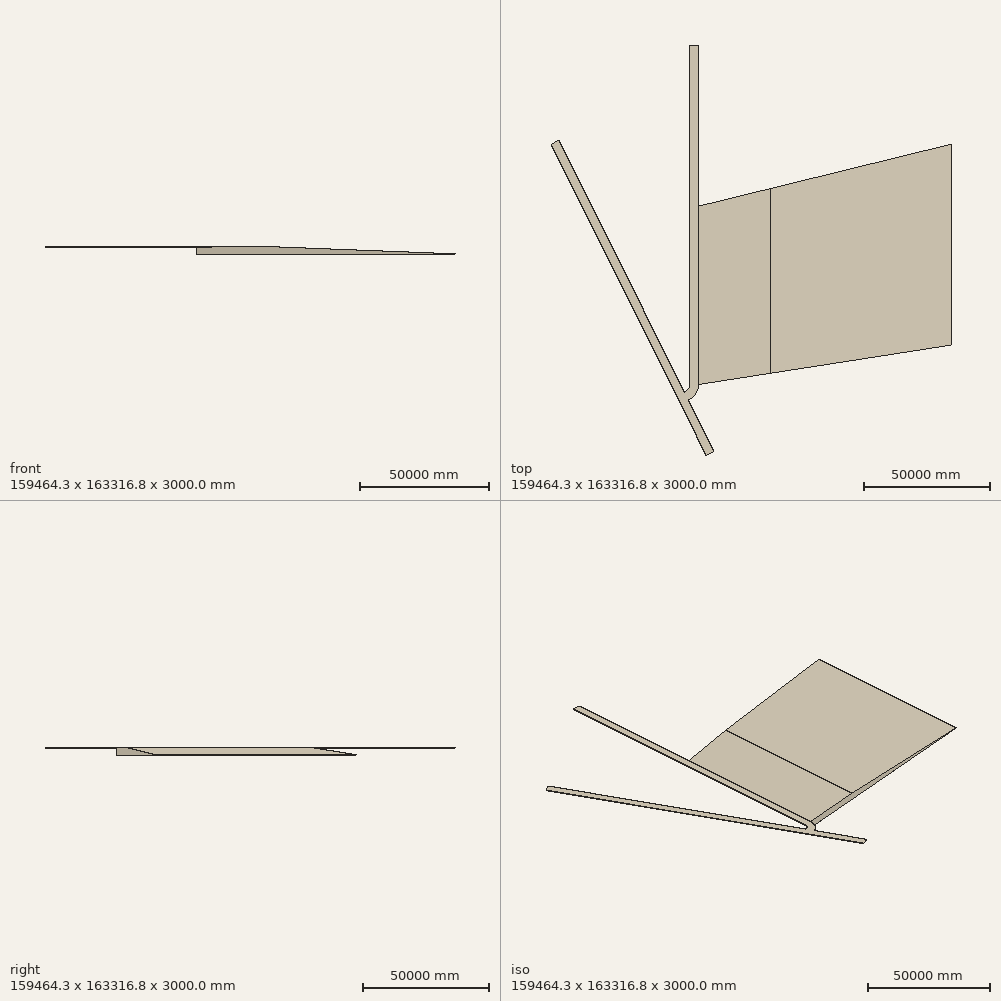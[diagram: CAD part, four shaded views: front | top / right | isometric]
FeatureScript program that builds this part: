
annotation { "Feature Type Name" : "Feature", "Feature Type Description" : "" }
export const myFeature = defineFeature(function(context is Context, id is Id, definition is map)
    precondition{}
    {
        {
            var Q0;
            Q0=qCreatedBy(makeId("Top.planeOp"),FACE);
            var sketch = newSketch(context, id + "F0", { "sketchPlane" : qUnion([Q0])});
            skLineSegment(sketch, "E0", {"start": v(0, 0) * mm, "end": v(0, 71000) * mm});
            skLineSegment(sketch, "E1", {"start": v(0, 0) * mm, "end": v(100779.6, 15731.25) * mm});
            skLineSegment(sketch, "E2", {"start": v(100779.6, 15731.25) * mm, "end": v(100779.6, 95731.25) * mm});
            skLineSegment(sketch, "E3", {"start": v(0, 71000) * mm, "end": v(100779.6, 95731.25) * mm});
            skLineSegment(sketch, "E4", {"start": v(0, 135054.72) * mm, "end": v(0, 71000) * mm});
            skArc(sketch, "E5", {"start": v(-4052.26, -6248.58) * mm, "mid": v(-1101.75, -3723.76) * mm, "end": v(0, 0) * mm});
            skLineSegment(sketch, "E6", {"start": v(-4052.26, -6248.58) * mm, "end": v(6144.3, -26700.48) * mm});
            skLineSegment(sketch, "E7", {"start": v(-3500, 18720.75) * mm, "end": v(-3500, 5971.3) * mm});
            skArc(sketch, "E8", {"start": v(-5616.78, -3110.52) * mm, "mid": v(-4079.4, -1881.23) * mm, "end": v(-3500, 0) * mm});
            skLineSegment(sketch, "E9", {"start": v(-3500, 5971.3) * mm, "end": v(-3500, 0) * mm});
            skLineSegment(sketch, "E10", {"start": v(-3500, 18720.75) * mm, "end": v(-3500, 135054.72) * mm});
            skLineSegment(sketch, "E11", {"start": v(6144.3, -26700.48) * mm, "end": v(3012.01, -28262.12) * mm});
            skLineSegment(sketch, "E12", {"start": v(3012.01, -28262.12) * mm, "end": v(-58684.68, 95486.93) * mm});
            skLineSegment(sketch, "E13", {"start": v(-5616.78, -3110.52) * mm, "end": v(-55719.75, 97384.26) * mm});
            skLineSegment(sketch, "E14", {"start": v(-58684.68, 95486.93) * mm, "end": v(-55719.75, 97384.26) * mm});
            skLineSegment(sketch, "E15", {"start": v(-3500, 135054.72) * mm, "end": v(0, 135054.72) * mm});
            skLineSegment(sketch, "E16", {"start": v(25000, 3902.39) * mm, "end": v(25000, 71552.82) * mm});
            skLineSegment(sketch, "E17", {"start": v(25000, 71552.82) * mm, "end": v(25000, 77134.98) * mm});
            skLineSegment(sketch, "E18", {"start": v(95000, 14829.08) * mm, "end": v(95000, 94312.94) * mm});
            skLineSegment(sketch, "E19", {"start": v(75000, 11707.17) * mm, "end": v(75000, 89404.95) * mm});
            skLineSegment(sketch, "E20", {"start": v(65000, 10146.21) * mm, "end": v(65000, 86950.96) * mm});
            skLineSegment(sketch, "E21", {"start": v(55000, 8585.26) * mm, "end": v(55000, 84496.97) * mm});
            skLineSegment(sketch, "E22", {"start": v(40000, 6243.82) * mm, "end": v(40000, 80815.97) * mm});
            skLineSegment(sketch, "E23", {"start": v(24900, 3886.78) * mm, "end": v(24900, 77110.44) * mm});
            skLineSegment(sketch, "E24", {"start": v(39900, 80791.43) * mm, "end": v(39900, 6228.21) * mm});
            skLineSegment(sketch, "E25", {"start": v(54900, 84472.43) * mm, "end": v(54900, 8569.65) * mm});
            skLineSegment(sketch, "E26", {"start": v(64900, 86926.42) * mm, "end": v(64900, 10130.6) * mm});
            skLineSegment(sketch, "E27", {"start": v(74900, 89380.41) * mm, "end": v(74900, 11691.56) * mm});
            skLineSegment(sketch, "E28", {"start": v(94900, 94288.4) * mm, "end": v(94900, 14813.47) * mm});
            skSolve(sketch);
        }
        {
            var Q0;
            Q0=makeQuery(id+"F0.imprint","IMPRINT",FACE,{"disambiguationData":[TD([[makeQuery(id+"F0.imprint","IMPRINT",EDGE,{"derivedFrom":sQuery(id+"F0.wireOp",EDGE,"E0")}),-1.0]])]});
            var Q1;
            {var subQ1=sQuery(id+"F0.wireOp",EDGE,"E16");Q1=makeQuery(id+"F0.imprint","IMPRINT",FACE,{"disambiguationData":[TD([[makeQuery(id+"F0.imprint","IMPRINT",EDGE,{"derivedFrom":subQ1}),-1.0]])]});}
            var Q2;
            {var subQ0=sQuery(id+"F0.wireOp",EDGE,"E22");Q2=makeQuery(id+"F0.imprint","IMPRINT",FACE,{"disambiguationData":[TD([[makeQuery(id+"F0.imprint","IMPRINT",EDGE,{"derivedFrom":subQ0}),-1.0]])]});}
            var Q3;
            {var subQ0=sQuery(id+"F0.wireOp",EDGE,"E21");Q3=makeQuery(id+"F0.imprint","IMPRINT",FACE,{"disambiguationData":[TD([[makeQuery(id+"F0.imprint","IMPRINT",EDGE,{"derivedFrom":subQ0}),-1.0]])]});}
            var Q4;
            {var subQ0=sQuery(id+"F0.wireOp",EDGE,"E20");Q4=makeQuery(id+"F0.imprint","IMPRINT",FACE,{"disambiguationData":[TD([[makeQuery(id+"F0.imprint","IMPRINT",EDGE,{"derivedFrom":subQ0}),-1.0]])]});}
            var Q5;
            {var subQ0=sQuery(id+"F0.wireOp",EDGE,"E19");Q5=makeQuery(id+"F0.imprint","IMPRINT",FACE,{"disambiguationData":[TD([[makeQuery(id+"F0.imprint","IMPRINT",EDGE,{"derivedFrom":subQ0}),-1.0]])]});}
            var Q6;
            {var subQ0=sQuery(id+"F0.wireOp",EDGE,"E2");Q6=makeQuery(id+"F0.imprint","IMPRINT",FACE,{"disambiguationData":[TD([[makeQuery(id+"F0.imprint","IMPRINT",EDGE,{"derivedFrom":subQ0}),1.0]])]});}
            var Q7;
            {var subQ0=sQuery(id+"F0.wireOp",EDGE,"E16");Q7=makeQuery(id+"F0.imprint","IMPRINT",FACE,{"disambiguationData":[TD([[makeQuery(id+"F0.imprint","IMPRINT",EDGE,{"derivedFrom":subQ0}),1.0]])]});}
            var Q8;
            {var subQ0=sQuery(id+"F0.wireOp",EDGE,"E22");Q8=makeQuery(id+"F0.imprint","IMPRINT",FACE,{"disambiguationData":[TD([[makeQuery(id+"F0.imprint","IMPRINT",EDGE,{"derivedFrom":subQ0}),1.0]])]});}
            var Q9;
            {var subQ0=sQuery(id+"F0.wireOp",EDGE,"E21");Q9=makeQuery(id+"F0.imprint","IMPRINT",FACE,{"disambiguationData":[TD([[makeQuery(id+"F0.imprint","IMPRINT",EDGE,{"derivedFrom":subQ0}),1.0]])]});}
            var Q10;
            {var subQ0=sQuery(id+"F0.wireOp",EDGE,"E20");Q10=makeQuery(id+"F0.imprint","IMPRINT",FACE,{"disambiguationData":[TD([[makeQuery(id+"F0.imprint","IMPRINT",EDGE,{"derivedFrom":subQ0}),1.0]])]});}
            var Q11;
            {var subQ0=sQuery(id+"F0.wireOp",EDGE,"E19");Q11=makeQuery(id+"F0.imprint","IMPRINT",FACE,{"disambiguationData":[TD([[makeQuery(id+"F0.imprint","IMPRINT",EDGE,{"derivedFrom":subQ0}),1.0]])]});}
            var Q12;
            {var subQ0=sQuery(id+"F0.wireOp",EDGE,"E18");Q12=makeQuery(id+"F0.imprint","IMPRINT",FACE,{"disambiguationData":[TD([[makeQuery(id+"F0.imprint","IMPRINT",EDGE,{"derivedFrom":subQ0}),1.0]])]});}
            extrude(context, id + "F1", {"entities" : qUnion([Q0, Q1, Q2, Q3, Q4, Q5, Q6, Q7, Q8, Q9, Q10, Q11, Q12]), "oppositeDirection" : true, "depth" : 3000 * mm, "offsetDistance" : 25 * mm});
        }
        {
            var Q0;
            Q0=makeQuery(id+"F1.opExtrude","CAP_EDGE",EDGE,{"disambiguationData":[OSD([sQuery(id+"F0.wireOp",EDGE,"E2")])],"isStart":true});
            chamfer(context, id + "F2", {"entities" : qUnion([Q0]), "chamferType" : ChamferType.TWO_OFFSETS, "width1" : 72000 * mm, "oppositeDirection" : false, "width2" : 2800 * mm, "tangentPropagation" : true});
        }
        {
            var Q0;
            Q0=makeQuery(id+"F0.imprint","IMPRINT",FACE,{"disambiguationData":[TD([[makeQuery(id+"F0.imprint","IMPRINT",EDGE,{"derivedFrom":sQuery(id+"F0.wireOp",EDGE,"E0")}),1.0]])]});
            extrude(context, id + "F3", {"entities" : qUnion([Q0]), "oppositeDirection" : true, "depth" : 200 * mm, "offsetDistance" : 25 * mm});
        }
    });
